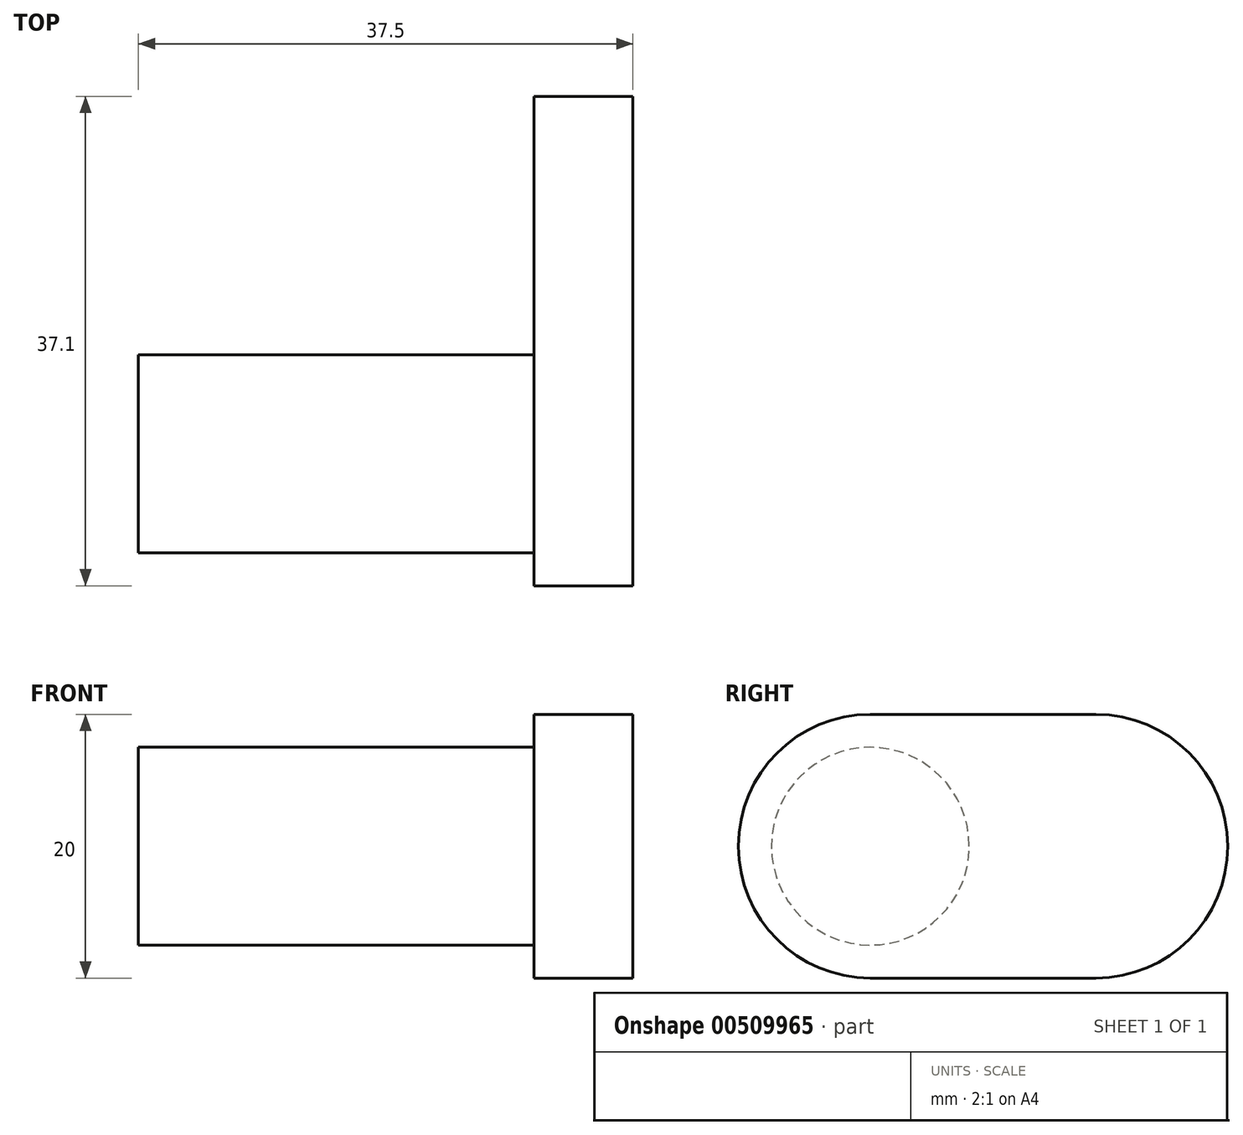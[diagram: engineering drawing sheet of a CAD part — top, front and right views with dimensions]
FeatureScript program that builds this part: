
annotation { "Feature Type Name" : "Feature", "Feature Type Description" : "" }
export const myFeature = defineFeature(function(context is Context, id is Id, definition is map)
    precondition{}
    {
        {
            var Q0;
            Q0=qCreatedBy(makeId("Right.planeOp"),FACE);
            var sketch = newSketch(context, id + "F0", { "sketchPlane" : qUnion([Q0])});
            skCircle(sketch, "E0", {"center": v(0, 0) * mm, "radius": 7.5 * mm});
            skSolve(sketch);
        }
        {
            var Q0;
            Q0 = qSketchRegion(id + "F0", true);
            extrude(context, id + "F1", {"entities" : qUnion([Q0]), "depth" : 30 * mm, "offsetDistance" : 25 * mm});
        }
        {
            var Q0;
            Q0=makeQuery(id+"F1.opExtrude","CAP_FACE",FACE,{"disambiguationData":[OSD([sQuery(id+"F0.wireOp",EDGE,"E0")])],"isStart":false});
            var sketch = newSketch(context, id + "F2", { "sketchPlane" : qUnion([Q0])});
            skArc(sketch, "E1", {"start": v(0, 10) * mm, "mid": v(-10, 0) * mm, "end": v(0, -10) * mm});
            skArc(sketch, "E2", {"start": v(17.1, -10) * mm, "mid": v(27.1, 0) * mm, "end": v(17.1, 10) * mm});
            skLineSegment(sketch, "E3", {"start": v(0, 10) * mm, "end": v(17.1, 10) * mm});
            skLineSegment(sketch, "E4", {"start": v(17.1, -10) * mm, "end": v(0, -10) * mm});
            skSolve(sketch);
        }
        {
            var Q0;
            Q0 = qSketchRegion(id + "F2", true);
            extrude(context, id + "F3", {"entities" : qUnion([Q0]), "operationType" : NewBodyOperationType.ADD, "depth" : 7.5 * mm, "offsetDistance" : 25 * mm});
        }
    });
